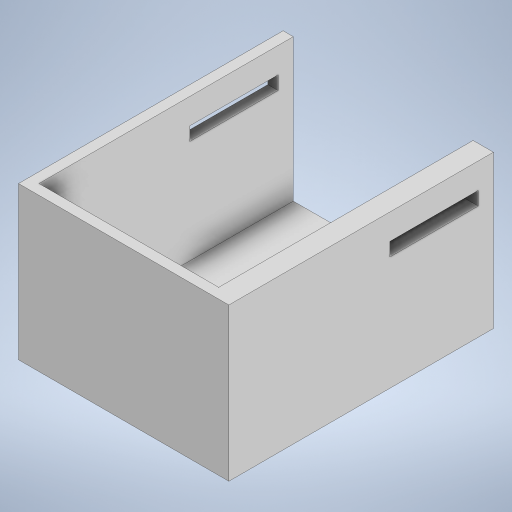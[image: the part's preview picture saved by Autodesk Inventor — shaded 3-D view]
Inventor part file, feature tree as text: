
AUTODESK INVENTOR PART (.ipt)
format: ipt  version: 2023 (Build 270158000, 158)  size: 245,248 bytes
history: native  units: in
note: dims shown in document units (in); Inventor stores cm internally (conversion verified against a paired STEP export)
features: sketch x5, extrude x4, shell x1
ambient origin geometry x8: Origin, YZ Plane, XZ Plane, XY Plane, X Axis, Y Axis, Z Axis, Center Point
bodies: Solid1 (feature_tree)
feature tree (10):
  extrude  "Extrusion1"  Depth=3.0709in
  shell  "Shell1"  Thickness=1.7717in
  sketch  "Sketch4"  dims[d4=0.1181in d17=0.3937in d18=0.0in]
  extrude  "Extrusion3"  Depth=0.1181in TaperAngle=0.0deg
  sketch  "Sketch6"  dims[d21=0.1772in d22=1.3189in]
  extrude  "Extrusion5"  Depth=0.1575in
  extrude  "Extrusion6"  Depth=1.3189in
  sketch  "Sketch2"  dims[d0=2.3228in d1=3.0709in d2=1.7717in d3=0.0in]
  sketch  "Sketch5"  dims[d19=1.0236in d20=0.1575in]
  sketch  "Sketch7"  dims[d25=0.1181in d26=0.0in d27=0.0in d28=0.0in d13=0.0197in d14=0.0344in d15=0.0197in d16=0.0344in]
